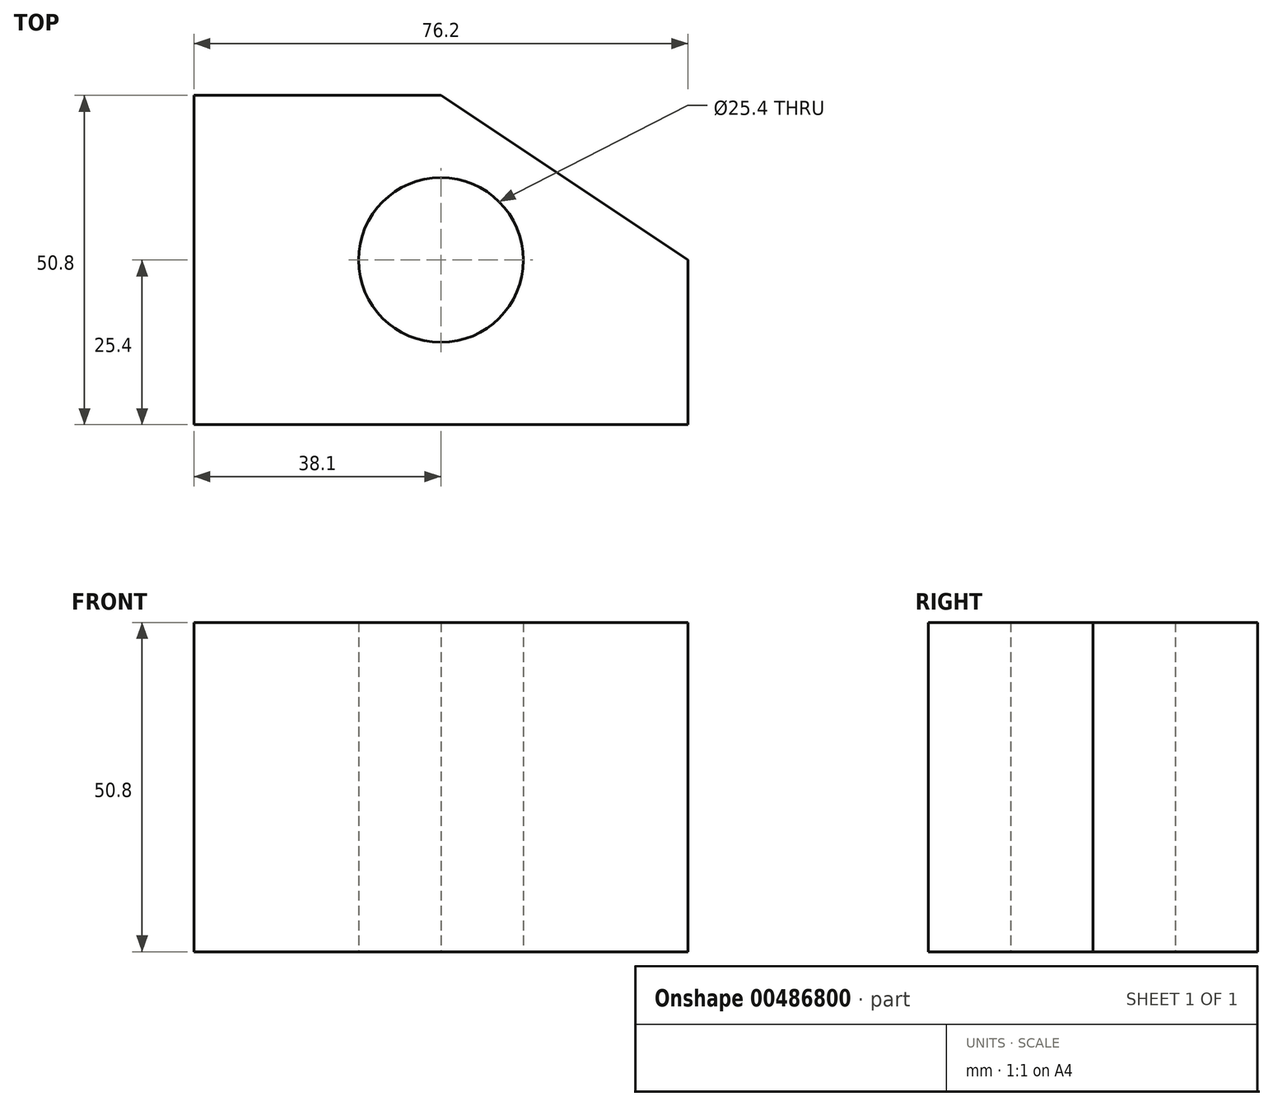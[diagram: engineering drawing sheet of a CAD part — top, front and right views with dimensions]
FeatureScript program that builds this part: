
annotation { "Feature Type Name" : "Feature", "Feature Type Description" : "" }
export const myFeature = defineFeature(function(context is Context, id is Id, definition is map)
    precondition{}
    {
        {
            var Q0;
            Q0=qCreatedBy(makeId("Top.planeOp"),FACE);
            var sketch = newSketch(context, id + "F0", { "sketchPlane" : qUnion([Q0])});
            skLineSegment(sketch, "E0.bottom", {"start": v(0, 0) * mm, "end": v(-76.2, 0) * mm});
            skLineSegment(sketch, "E0.top", {"start": v(0, 50.8) * mm, "end": v(-76.2, 50.8) * mm});
            skLineSegment(sketch, "E0.left", {"start": v(0, 0) * mm, "end": v(0, 50.8) * mm});
            skLineSegment(sketch, "E0.right", {"start": v(-76.2, 0) * mm, "end": v(-76.2, 50.8) * mm});
            skCircle(sketch, "E1", {"center": v(-38.1, 25.4) * mm, "radius": 12.7 * mm});
            skLineSegment(sketch, "E2", {"start": v(-38.1, 50.8) * mm, "end": v(0, 25.4) * mm});
            skSolve(sketch);
        }
        {
            var Q0;
            Q0=makeQuery(id+"F0.imprint","IMPRINT",FACE,{"disambiguationData":[TD([[makeQuery(id+"F0.imprint","IMPRINT",EDGE,{"derivedFrom":sQuery(id+"F0.wireOp",EDGE,"E0.bottom")}),-1.0]])]});
            extrude(context, id + "F1", {"entities" : qUnion([Q0]), "depth" : 50.8 * mm});
        }
    });
